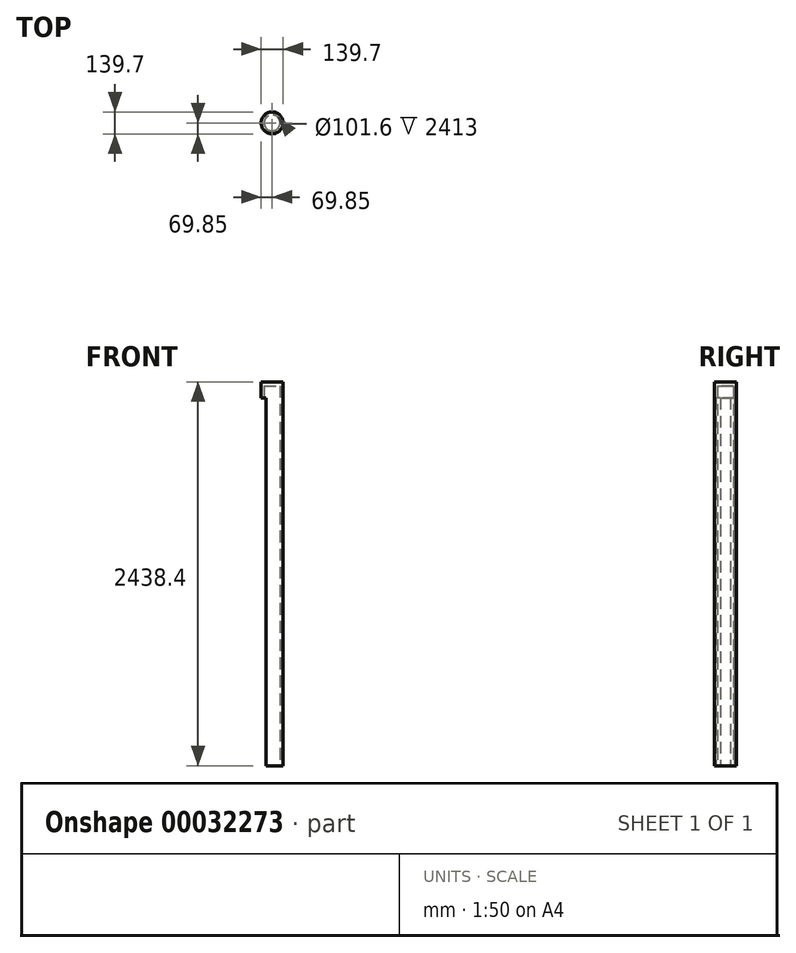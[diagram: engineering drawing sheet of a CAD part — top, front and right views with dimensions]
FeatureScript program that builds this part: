
annotation { "Feature Type Name" : "Feature", "Feature Type Description" : "" }
export const myFeature = defineFeature(function(context is Context, id is Id, definition is map)
    precondition{}
    {
        {
            var Q0;
            Q0=qCreatedBy(makeId("Top.planeOp"),FACE);
            var sketch = newSketch(context, id + "F0", { "sketchPlane" : qUnion([Q0])});
            skCircle(sketch, "E0", {"center": v(0, 0) * mm, "radius": 69.85 * mm});
            skSolve(sketch);
        }
        {
            var Q0;
            Q0=makeQuery(id+"F0.imprint","IMPRINT",FACE,{"disambiguationData":[TD([[makeQuery(id+"F0.imprint","IMPRINT",EDGE,{"derivedFrom":sQuery(id+"F0.wireOp",EDGE,"E0")}),1.0]])]});
            extrude(context, id + "F1", {"entities" : qUnion([Q0]), "depth" : 2438.4 * mm});
        }
        {
            var Q0;
            Q0=makeQuery(id+"F1.opExtrude","CAP_FACE",FACE,{"disambiguationData":[OSD([sQuery(id+"F0.wireOp",EDGE,"E0")])],"isStart":true});
            var sketch = newSketch(context, id + "F2", { "sketchPlane" : qUnion([Q0])});
            skCircle(sketch, "E1", {"center": v(0, 0) * mm, "radius": 50.8 * mm});
            skSolve(sketch);
        }
        {
            var Q0;
            Q0=makeQuery(id+"F2.imprint","IMPRINT",FACE,{"disambiguationData":[TD([[makeQuery(id+"F2.imprint","IMPRINT",EDGE,{"derivedFrom":sQuery(id+"F2.wireOp",EDGE,"E1")}),1.0]])]});
            extrude(context, id + "F3", {"entities" : qUnion([Q0]), "operationType" : NewBodyOperationType.REMOVE, "oppositeDirection" : true, "depth" : 2413 * mm});
        }
        {
            var Q0;
            Q0=makeQuery(id+"F1.opExtrude","CAP_FACE",FACE,{"disambiguationData":[OSD([sQuery(id+"F0.wireOp",EDGE,"E0")])],"isStart":true});
            var sketch = newSketch(context, id + "F4", { "sketchPlane" : qUnion([Q0])});
            skArc(sketch, "E2", {"start": v(-39.66, 57.5) * mm, "mid": v(-69.85, 0) * mm, "end": v(-39.66, -57.5) * mm});
            skLineSegment(sketch, "E3", {"start": v(-39.66, 31.75) * mm, "end": v(-39.66, -31.75) * mm});
            skLineSegment(sketch, "E4", {"start": v(-39.66, 31.75) * mm, "end": v(-39.66, 57.5) * mm});
            skLineSegment(sketch, "E5", {"start": v(-39.66, -31.75) * mm, "end": v(-39.66, -57.5) * mm});
            skSolve(sketch);
        }
        {
            var Q0;
            Q0=makeQuery(id+"F4.imprint","IMPRINT",FACE,{"disambiguationData":[TD([[makeQuery(id+"F4.imprint","IMPRINT",EDGE,{"derivedFrom":sQuery(id+"F4.wireOp",EDGE,"E2")}),-1.0]])]});
            extrude(context, id + "F5", {"entities" : qUnion([Q0]), "operationType" : NewBodyOperationType.REMOVE, "oppositeDirection" : true, "depth" : 2336.8 * mm});
        }
    });
